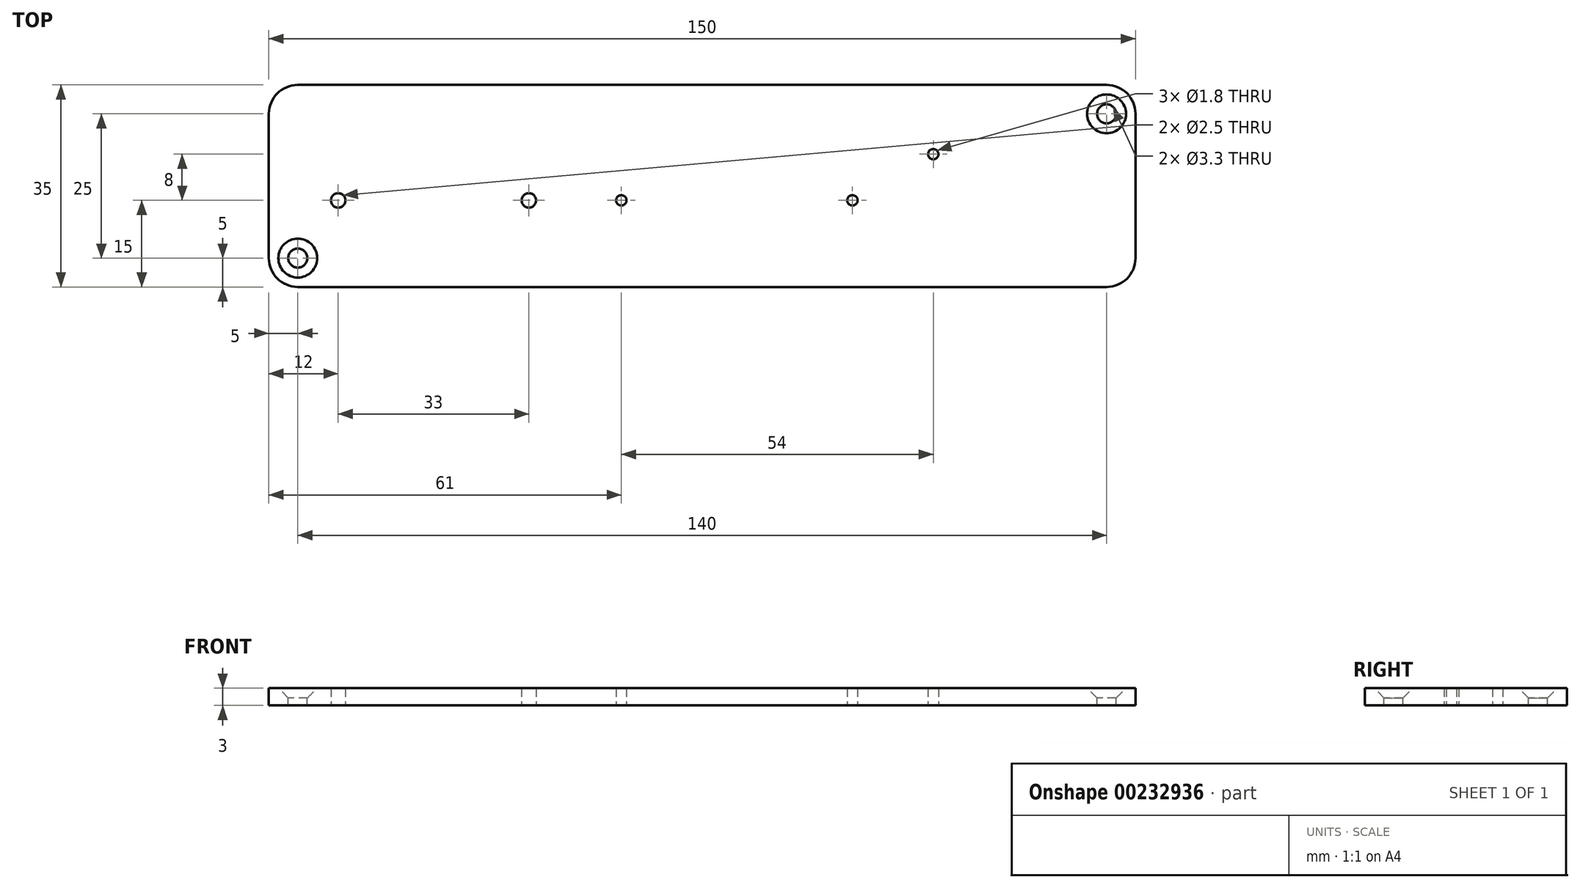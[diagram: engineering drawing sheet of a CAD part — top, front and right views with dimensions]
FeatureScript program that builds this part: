
annotation { "Feature Type Name" : "Feature", "Feature Type Description" : "" }
export const myFeature = defineFeature(function(context is Context, id is Id, definition is map)
    precondition{}
    {
        {
            var Q0;
            Q0=qCreatedBy(makeId("Top.planeOp"),FACE);
            var sketch = newSketch(context, id + "F0", { "sketchPlane" : qUnion([Q0])});
            skLineSegment(sketch, "E0.bottom", {"start": v(0, 0) * mm, "end": v(150, 0) * mm});
            skLineSegment(sketch, "E0.top", {"start": v(0, 35) * mm, "end": v(150, 35) * mm});
            skLineSegment(sketch, "E0.left", {"start": v(0, 0) * mm, "end": v(0, 35) * mm});
            skLineSegment(sketch, "E0.right", {"start": v(150, 0) * mm, "end": v(150, 35) * mm});
            skLineSegment(sketch, "E1", {"start": v(0, 15) * mm, "end": v(150, 15) * mm, "construction": true});
            skPoint(sketch, "E2", {"position": v(101, 15) * mm});
            skPoint(sketch, "E3", {"position": v(61, 15) * mm});
            skPoint(sketch, "E4", {"position": v(45, 15) * mm});
            skPoint(sketch, "E5", {"position": v(12, 15) * mm});
            skPoint(sketch, "E6", {"position": v(101, 23) * mm});
            skPoint(sketch, "E7", {"position": v(115, 23) * mm});
            skCircle(sketch, "E8", {"center": v(115, 23) * mm, "radius": 0.9 * mm});
            skCircle(sketch, "E9", {"center": v(101, 15) * mm, "radius": 0.9 * mm});
            skCircle(sketch, "E10", {"center": v(61, 15) * mm, "radius": 0.9 * mm});
            skCircle(sketch, "E11", {"center": v(12, 15) * mm, "radius": 1.25 * mm});
            skCircle(sketch, "E12", {"center": v(45, 15) * mm, "radius": 1.25 * mm});
            skPoint(sketch, "E13", {"position": v(0, 35) * mm});
            skLineSegment(sketch, "E14", {"start": v(150, 0) * mm, "end": v(0, 35) * mm, "construction": true});
            skPoint(sketch, "E15", {"position": v(5, 3.3) * mm});
            skPoint(sketch, "E16", {"position": v(145, 30) * mm});
            skSolve(sketch);
        }
        {
            var Q0;
            Q0=makeQuery(id+"F0.imprint","IMPRINT",FACE,{"disambiguationData":[TD([[makeQuery(id+"F0.imprint","IMPRINT",EDGE,{"derivedFrom":sQuery(id+"F0.wireOp",EDGE,"E0.bottom")}),1.0]])]});
            extrude(context, id + "F1", {"entities" : qUnion([Q0]), "depth" : 3 * mm});
        }
        {
            var Q0;
            Q0=makeQuery(id+"F1.opExtrude","SWEPT_EDGE",EDGE,{"disambiguationData":[OSD([sQuery(id+"F0.wireOp",EDGE,"E0.top"),sQuery(id+"F0.wireOp",EDGE,"E0.left")])]});
            var Q1;
            Q1=makeQuery(id+"F1.opExtrude","SWEPT_EDGE",EDGE,{"disambiguationData":[OSD([sQuery(id+"F0.wireOp",EDGE,"E0.bottom"),sQuery(id+"F0.wireOp",EDGE,"E0.left")])]});
            var Q2;
            Q2=makeQuery(id+"F1.opExtrude","SWEPT_EDGE",EDGE,{"disambiguationData":[OSD([sQuery(id+"F0.wireOp",EDGE,"E0.bottom"),sQuery(id+"F0.wireOp",EDGE,"E0.right")])]});
            var Q3;
            Q3=makeQuery(id+"F1.opExtrude","SWEPT_EDGE",EDGE,{"disambiguationData":[OSD([sQuery(id+"F0.wireOp",EDGE,"E0.top"),sQuery(id+"F0.wireOp",EDGE,"E0.right")])]});
            fillet(context, id + "F2", {"entities" : qUnion([Q0, Q1, Q2, Q3]), "radius" : 5 * mm, "tangentPropagation" : true, "allowEdgeOverflow" : false});
        }
        {
            var Q0;
            Q0=makeQuery(id+"F1.opExtrude","CAP_FACE",FACE,{"disambiguationData":[OSD([sQuery(id+"F0.wireOp",EDGE,"E0.bottom"),sQuery(id+"F0.wireOp",EDGE,"E0.top"),sQuery(id+"F0.wireOp",EDGE,"E0.left"),sQuery(id+"F0.wireOp",EDGE,"E0.right"),sQuery(id+"F0.wireOp",EDGE,"E8"),sQuery(id+"F0.wireOp",EDGE,"E9"),sQuery(id+"F0.wireOp",EDGE,"E10"),sQuery(id+"F0.wireOp",EDGE,"E11"),sQuery(id+"F0.wireOp",EDGE,"E12")])],"isStart":false});
            var sketch = newSketch(context, id + "F3", { "sketchPlane" : qUnion([Q0])});
            skPoint(sketch, "E17", {"position": v(5, 5) * mm});
            skPoint(sketch, "E18", {"position": v(145, 30) * mm});
            skSolve(sketch);
        }
        {
            var Q0;
            Q0=sQuery(id+"F3.wireOp",VERTEX,"E17");
            var Q1;
            Q1=sQuery(id+"F3.wireOp",VERTEX,"E18");
            var Q2;
            Q2=makeQuery(id+"F1.opExtrude","SWEPT_BODY",BODY,{"disambiguationData":[OSD([sQuery(id+"F0.wireOp",EDGE,"E0.bottom"),sQuery(id+"F0.wireOp",EDGE,"E0.top"),sQuery(id+"F0.wireOp",EDGE,"E0.left"),sQuery(id+"F0.wireOp",EDGE,"E0.right"),sQuery(id+"F0.wireOp",EDGE,"E8"),sQuery(id+"F0.wireOp",EDGE,"E9"),sQuery(id+"F0.wireOp",EDGE,"E10"),sQuery(id+"F0.wireOp",EDGE,"E11"),sQuery(id+"F0.wireOp",EDGE,"E12")])]});
            hole(context, id + "F4", {"style" : HoleStyle.C_SINK, "endStyle" : HoleEndStyle.THROUGH, "standardTappedOrClearance" : lookupTablePath({ "standard" : "ISO", "fit" : "Normal", "size" : "M3", "type" : "Clearance" }), "standardBlindInLast" : lookupTablePath({ "fit" : "Standard", "standard" : "ISO", "size" : "M3", "type" : "Clearance" }), "holeDiameter" : 3.3 * mm, "cSinkDiameter" : 6.72 * mm, "cSinkAngle" : 90 * degree, "tappedDepth" : 12 * mm, "tapClearance" : 3, "locations" : qUnion([Q0, Q1]), "scope" : qUnion([Q2])});
        }
    });
